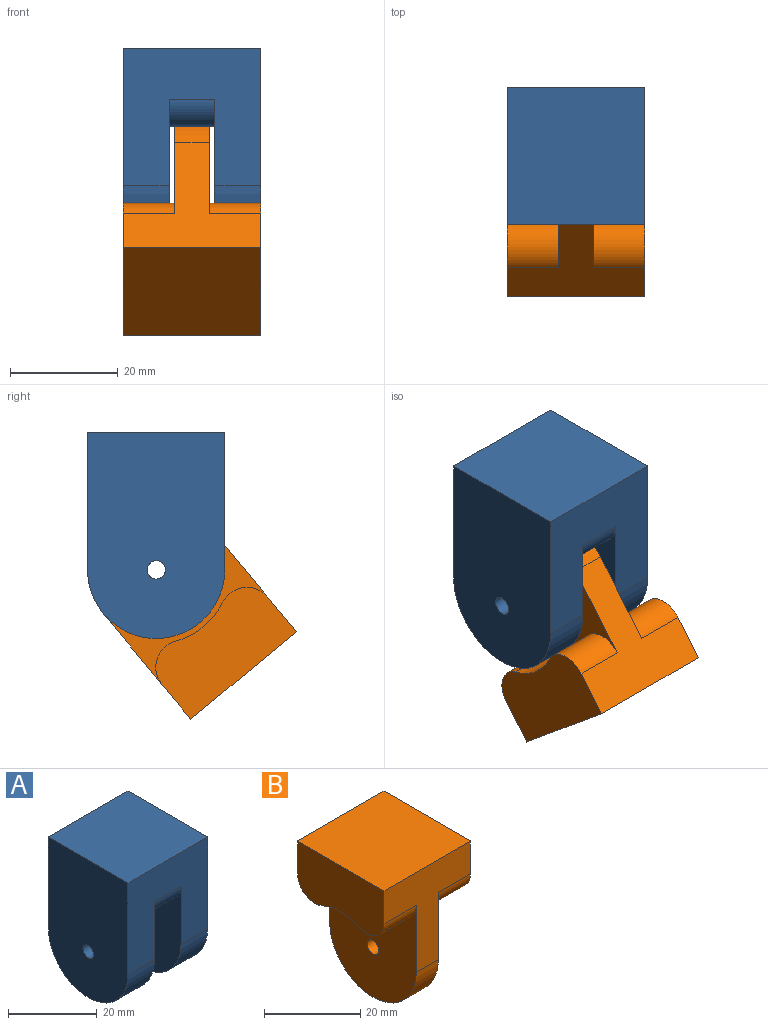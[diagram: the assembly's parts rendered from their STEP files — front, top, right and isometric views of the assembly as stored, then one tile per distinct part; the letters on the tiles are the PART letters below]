
ASSEMBLY  parts=2 mates=1
PART A: 14 faces, bbox 25.4x25.4x38.1 mm
  f0: plane 25.4x25.4mm, normal (0,-1,0), area 510.2mm2, adj f1,f3,f4,f5,f6,f7,f8,f11
  f1: plane 38.1x25.4mm, normal (1,0,0), area 889.4mm2, adj f0,f2,f4,f8,f12
  f2: plane 25.4x25.4mm, normal (0,1,0), area 510.2mm2, adj f1,f3,f4,f5,f6,f7,f8,f10
  f3: plane 38.1x25.4mm, normal (-1,0,0), area 889.4mm2, adj f0,f2,f4,f5,f13
  f4: plane 25.4x25.4mm, normal (0,0,1), area 645.2mm2, adj f0,f1,f2,f3
  f5: cylinder r=12.7mm len=25.4mm, axis (-1,0,0), area 337.8mm2, adj f0,f2,f3,f6
  f6: plane 28.64x25.4mm, normal (1,0,0), area 548.4mm2, adj f0,f2,f5,f9,f10,f11,f13
  f7: plane 28.64x25.4mm, normal (-1,0,0), area 548.4mm2, adj f0,f2,f8,f9,f10,f11,f12
  f8: cylinder r=12.7mm len=25.4mm, axis (-1,0,0), area 337.8mm2, adj f0,f1,f2,f7
  f9: cylinder r=12.7mm len=11.05mm, axis (1,0,0), area 96.8mm2, adj f6,f7,f10,f11
  f10: cylinder r=5mm len=8.47mm, axis (1,0,0), area 85.5mm2, adj f2,f6,f7,f9
  f11: cylinder r=5mm len=8.47mm, axis (1,0,0), area 85.5mm2, adj f0,f6,f7,f9
  f12: cylinder r=1.7mm len=8.47mm, axis (-1,0,0), area 90.4mm2, adj f1,f7
  f13: cylinder r=1.7mm len=8.47mm, axis (-1,0,0), area 90.4mm2, adj f3,f6
PART B: 15 faces, bbox 25.4x25.4x38.1 mm
  f0: plane 25.4x25.4mm, normal (0,1,0), area 322.5mm2, adj f1,f2,f3,f5,f10,f11,f12,f13
  f1: cylinder r=12.7mm len=25.4mm, axis (1,0,0), area 258mm2, adj f0,f4,f12,f13
  f2: plane 25.4x13.36mm, normal (1,0,0), area 313.8mm2, adj f0,f4,f5,f7,f8,f10
  f3: plane 25.4x13.36mm, normal (-1,0,0), area 313.8mm2, adj f0,f4,f5,f6,f9,f11
  f4: plane 25.4x25.4mm, normal (0,-1,0), area 322.5mm2, adj f1,f2,f3,f5,f8,f9,f12,f13
  f5: plane 25.4x25.4mm, normal (0,0,1), area 645.2mm2, adj f0,f2,f3,f4
  f6: cylinder r=13.7mm len=11.28mm, axis (-1,0,0), area 110.1mm2, adj f3,f9,f11,f12
  f7: cylinder r=13.7mm len=11.28mm, axis (-1,0,0), area 110.1mm2, adj f2,f8,f10,f13
  f8: cylinder r=5mm len=9.47mm, axis (-1,0,0), area 94.4mm2, adj f2,f4,f7,f13
  f9: cylinder r=5mm len=9.47mm, axis (-1,0,0), area 94.4mm2, adj f3,f4,f6,f12
  f10: cylinder r=5mm len=9.47mm, axis (-1,0,0), area 94.4mm2, adj f0,f2,f7,f13
  f11: cylinder r=5mm len=9.47mm, axis (-1,0,0), area 94.4mm2, adj f0,f3,f6,f12
  f12: plane 29.74x25.4mm, normal (-1,0,0), area 575.7mm2, adj f0,f1,f4,f6,f9,f11,f14
  f13: plane 29.74x25.4mm, normal (1,0,0), area 575.7mm2, adj f0,f1,f4,f7,f8,f10,f14
  f14: cylinder r=1.7mm len=6.47mm, axis (-1,0,0), area 69.1mm2, adj f12,f13
PLACE A at identity fixed
PLACE B rot(axis=(1,0,0),140.4deg) t=(0,0,0)mm
MATE revolute A.f12 <-> B.f1  axis (-1,0,0) through (0,0,0)mm
